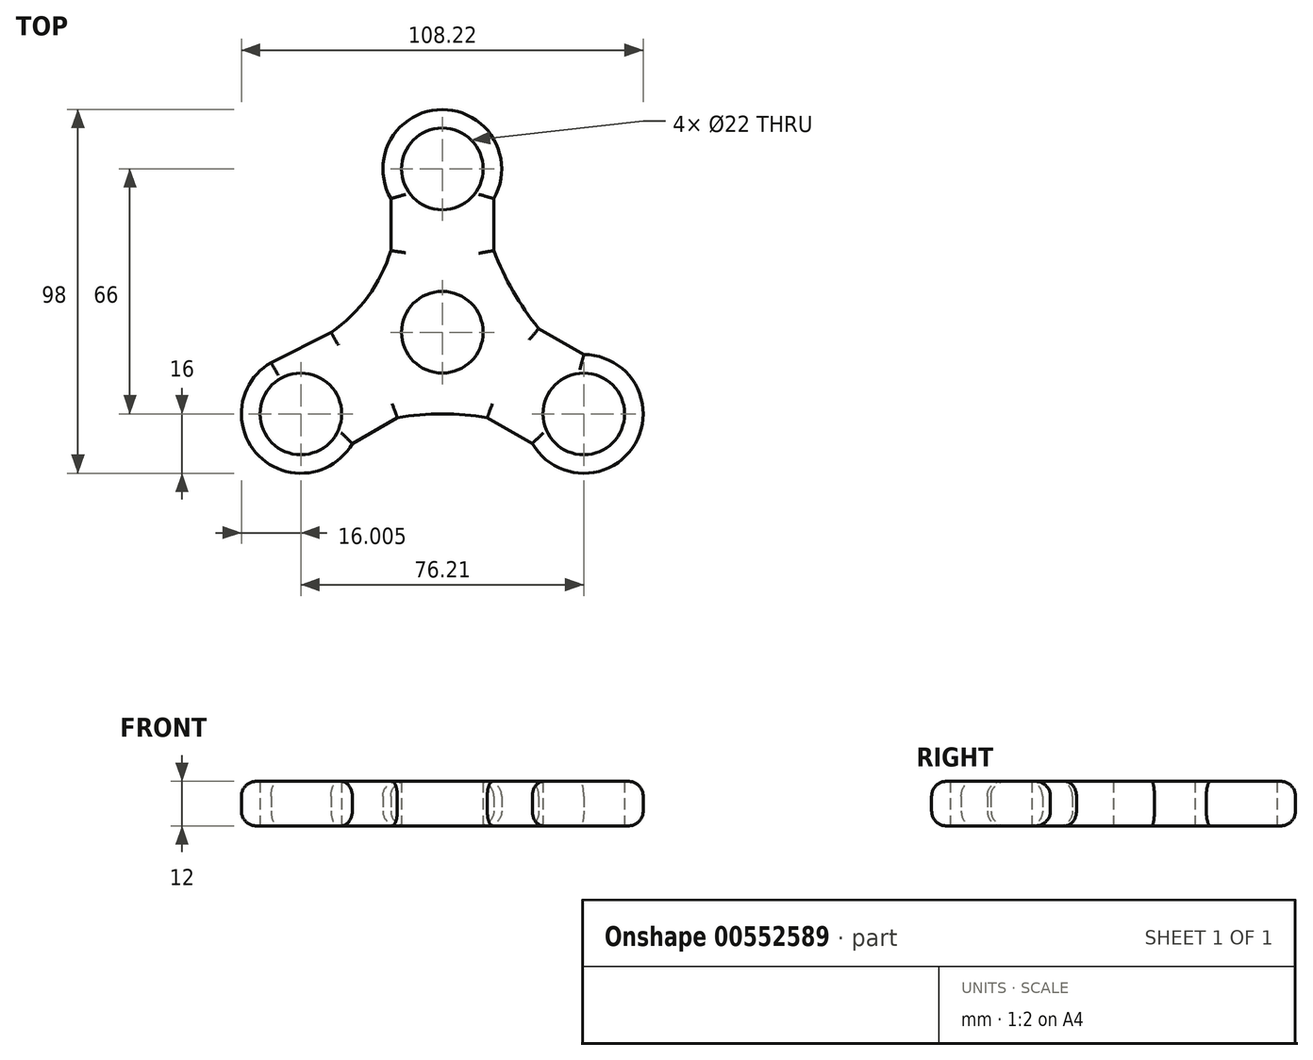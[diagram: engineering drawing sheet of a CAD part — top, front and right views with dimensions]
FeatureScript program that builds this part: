
annotation { "Feature Type Name" : "Feature", "Feature Type Description" : "" }
export const myFeature = defineFeature(function(context is Context, id is Id, definition is map)
    precondition{}
    {
        {
            var Q0;
            Q0=qCreatedBy(makeId("Top.planeOp"),FACE);
            var sketch = newSketch(context, id + "F0", { "sketchPlane" : qUnion([Q0])});
            skCircle(sketch, "E0", {"center": v(0, 0) * mm, "radius": 11 * mm});
            skLineSegment(sketch, "E1", {"start": v(0, 0) * mm, "end": v(0, 44) * mm, "construction": true});
            skCircle(sketch, "E2", {"center": v(0, 44) * mm, "radius": 11 * mm});
            skLineSegment(sketch, "E3", {"start": v(-38.1, -22) * mm, "end": v(0, 0) * mm, "construction": true});
            skLineSegment(sketch, "E4", {"start": v(38.1, -22) * mm, "end": v(0, 0) * mm, "construction": true});
            skLineSegment(sketch, "E5", {"start": v(38.1, -22) * mm, "end": v(-38.1, -22) * mm, "construction": true});
            skCircle(sketch, "E6", {"center": v(-38.1, -22) * mm, "radius": 11 * mm});
            skCircle(sketch, "E7", {"center": v(38.1, -22) * mm, "radius": 11 * mm});
            skLineSegment(sketch, "E8", {"start": v(0, 44) * mm, "end": v(-38.1, -22) * mm, "construction": true});
            skLineSegment(sketch, "E9", {"start": v(38.1, -22) * mm, "end": v(0, 44) * mm, "construction": true});
            skCircle(sketch, "E10", {"center": v(-38.1, -22) * mm, "radius": 16 * mm, "construction": true});
            skCircle(sketch, "E11", {"center": v(0, 44) * mm, "radius": 16 * mm, "construction": true});
            skCircle(sketch, "E12", {"center": v(38.1, -22) * mm, "radius": 16 * mm, "construction": true});
            skLineSegment(sketch, "E13", {"start": v(-38.1, -22) * mm, "end": v(-38.1, -6) * mm, "construction": true});
            skLineSegment(sketch, "E14", {"start": v(-38.1, -22) * mm, "end": v(-46.1, -8.14) * mm, "construction": true});
            skLineSegment(sketch, "E15", {"start": v(-38.1, -22) * mm, "end": v(-24.25, -30) * mm, "construction": true});
            skArc(sketch, "E16", {"start": v(-46.1, -8.14) * mm, "mid": v(-49.42, -33.31) * mm, "end": v(-24.25, -30) * mm});
            skLineSegment(sketch, "E17", {"start": v(0, 44) * mm, "end": v(-16, 44) * mm, "construction": true});
            skLineSegment(sketch, "E18", {"start": v(0, 44) * mm, "end": v(16, 44) * mm, "construction": true});
            skLineSegment(sketch, "E19", {"start": v(0, 44) * mm, "end": v(-13.86, 36) * mm, "construction": true});
            skCircle(sketch, "E20", {"center": v(0, 0) * mm, "radius": 16 * mm, "construction": true});
            skLineSegment(sketch, "E21", {"start": v(0, 44) * mm, "end": v(13.86, 36) * mm, "construction": true});
            skArc(sketch, "E22", {"start": v(13.86, 36) * mm, "mid": v(0, 60) * mm, "end": v(-13.86, 36) * mm});
            skLineSegment(sketch, "E23", {"start": v(38.1, -22) * mm, "end": v(38.1, -6) * mm, "construction": true});
            skLineSegment(sketch, "E24", {"start": v(38.1, -22) * mm, "end": v(24.25, -30) * mm, "construction": true});
            skArc(sketch, "E25", {"start": v(24.25, -30) * mm, "mid": v(51.96, -30) * mm, "end": v(38.1, -6) * mm});
            skLineSegment(sketch, "E26", {"start": v(-19.05, 11) * mm, "end": v(-13.86, 8) * mm, "construction": true});
            skLineSegment(sketch, "E27", {"start": v(19.05, 11) * mm, "end": v(13.86, 8) * mm, "construction": true});
            skLineSegment(sketch, "E28", {"start": v(0, -22) * mm, "end": v(0, -16) * mm, "construction": true});
            skLineSegment(sketch, "E29", {"start": v(-46.1, -8.14) * mm, "end": v(-13.86, 8) * mm});
            skLineSegment(sketch, "E30", {"start": v(-13.86, 8) * mm, "end": v(-13.86, 36) * mm});
            skLineSegment(sketch, "E31", {"start": v(13.86, 36) * mm, "end": v(13.86, 8) * mm});
            skLineSegment(sketch, "E32", {"start": v(13.86, 8) * mm, "end": v(38.1, -6) * mm});
            skLineSegment(sketch, "E33", {"start": v(24.25, -30) * mm, "end": v(0, -16) * mm});
            skLineSegment(sketch, "E34", {"start": v(0, -16) * mm, "end": v(-24.25, -30) * mm});
            skArc(sketch, "E35", {"start": v(-29.98, -0.07) * mm, "mid": v(-20.04, 9.6) * mm, "end": v(-13.86, 22) * mm});
            skArc(sketch, "E36", {"start": v(13.86, 22) * mm, "mid": v(19.05, 11) * mm, "end": v(25.98, 1) * mm});
            skArc(sketch, "E37", {"start": v(12.12, -23) * mm, "mid": v(0, -22) * mm, "end": v(-12.12, -23) * mm});
            skSolve(sketch);
        }
        {
            var Q0;
            Q0=makeQuery(id+"F0.imprint","IMPRINT",FACE,{"disambiguationData":[TD([[makeQuery(id+"F0.imprint","IMPRINT",EDGE,{"derivedFrom":sQuery(id+"F0.wireOp",EDGE,"E0")}),-1.0]])]});
            var Q1;
            {var subQ3=sQuery(id+"F0.wireOp",EDGE,"E37");Q1=makeQuery(id+"F0.imprint","IMPRINT",FACE,{"disambiguationData":[TD([[makeQuery(id+"F0.imprint","IMPRINT",EDGE,{"derivedFrom":subQ3}),-1.0]])]});}
            var Q2;
            {var subQ3=sQuery(id+"F0.wireOp",EDGE,"E35");Q2=makeQuery(id+"F0.imprint","IMPRINT",FACE,{"disambiguationData":[TD([[makeQuery(id+"F0.imprint","IMPRINT",EDGE,{"derivedFrom":subQ3}),-1.0]])]});}
            var Q3;
            {var subQ3=sQuery(id+"F0.wireOp",EDGE,"E36");Q3=makeQuery(id+"F0.imprint","IMPRINT",FACE,{"disambiguationData":[TD([[makeQuery(id+"F0.imprint","IMPRINT",EDGE,{"derivedFrom":subQ3}),-1.0]])]});}
            extrude(context, id + "F1", {"entities" : qUnion([Q0, Q1, Q2, Q3]), "depth" : 12 * mm, "offsetDistance" : 25 * mm});
        }
        {
            var Q0;
            Q0=makeQuery(id+"F1.opExtrude","CAP_EDGE",EDGE,{"disambiguationData":[OSD([sQuery(id+"F0.wireOp",EDGE,"E29")])],"isStart":false});
            var Q1;
            Q1=makeQuery(id+"F1.opExtrude","CAP_EDGE",EDGE,{"disambiguationData":[OSD([sQuery(id+"F0.wireOp",EDGE,"E34")])],"isStart":false});
            var Q2;
            Q2=makeQuery(id+"F1.opExtrude","CAP_EDGE",EDGE,{"disambiguationData":[OSD([sQuery(id+"F0.wireOp",EDGE,"E16")])],"isStart":false});
            var Q3;
            Q3=makeQuery(id+"F1.opExtrude","CAP_EDGE",EDGE,{"disambiguationData":[OSD([sQuery(id+"F0.wireOp",EDGE,"E25")])],"isStart":false});
            var Q4;
            Q4=makeQuery(id+"F1.opExtrude","CAP_EDGE",EDGE,{"disambiguationData":[OSD([sQuery(id+"F0.wireOp",EDGE,"E33")])],"isStart":false});
            var Q5;
            Q5=makeQuery(id+"F1.opExtrude","CAP_EDGE",EDGE,{"disambiguationData":[OSD([sQuery(id+"F0.wireOp",EDGE,"E32")])],"isStart":false});
            var Q6;
            Q6=makeQuery(id+"F1.opExtrude","CAP_EDGE",EDGE,{"disambiguationData":[OSD([sQuery(id+"F0.wireOp",EDGE,"E31")])],"isStart":false});
            var Q7;
            Q7=makeQuery(id+"F1.opExtrude","CAP_EDGE",EDGE,{"disambiguationData":[OSD([sQuery(id+"F0.wireOp",EDGE,"E22")])],"isStart":false});
            var Q8;
            Q8=makeQuery(id+"F1.opExtrude","CAP_EDGE",EDGE,{"disambiguationData":[OSD([sQuery(id+"F0.wireOp",EDGE,"E32")])],"isStart":true});
            var Q9;
            Q9=makeQuery(id+"F1.opExtrude","CAP_EDGE",EDGE,{"disambiguationData":[OSD([sQuery(id+"F0.wireOp",EDGE,"E29")])],"isStart":true});
            var Q10;
            Q10=makeQuery(id+"F1.opExtrude","CAP_EDGE",EDGE,{"disambiguationData":[OSD([sQuery(id+"F0.wireOp",EDGE,"E16")])],"isStart":true});
            var Q11;
            Q11=makeQuery(id+"F1.opExtrude","CAP_EDGE",EDGE,{"disambiguationData":[OSD([sQuery(id+"F0.wireOp",EDGE,"E34")])],"isStart":true});
            var Q12;
            Q12=makeQuery(id+"F1.opExtrude","CAP_EDGE",EDGE,{"disambiguationData":[OSD([sQuery(id+"F0.wireOp",EDGE,"E33")])],"isStart":true});
            var Q13;
            Q13=makeQuery(id+"F1.opExtrude","CAP_EDGE",EDGE,{"disambiguationData":[OSD([sQuery(id+"F0.wireOp",EDGE,"E25")])],"isStart":true});
            var Q14;
            Q14=makeQuery(id+"F1.opExtrude","CAP_EDGE",EDGE,{"disambiguationData":[OSD([sQuery(id+"F0.wireOp",EDGE,"E22")])],"isStart":true});
            var Q15;
            Q15=makeQuery(id+"F1.opExtrude","CAP_EDGE",EDGE,{"disambiguationData":[OSD([sQuery(id+"F0.wireOp",EDGE,"E31")])],"isStart":true});
            var Q16;
            Q16=makeQuery(id+"F1.opExtrude","CAP_EDGE",EDGE,{"disambiguationData":[OSD([sQuery(id+"F0.wireOp",EDGE,"E37")])],"isStart":false});
            var Q17;
            Q17=makeQuery(id+"F1.opExtrude","CAP_EDGE",EDGE,{"disambiguationData":[OSD([sQuery(id+"F0.wireOp",EDGE,"E35")])],"isStart":false});
            var Q18;
            Q18=makeQuery(id+"F1.opExtrude","CAP_EDGE",EDGE,{"disambiguationData":[OSD([sQuery(id+"F0.wireOp",EDGE,"E36")])],"isStart":false});
            var Q19;
            Q19=makeQuery(id+"F1.opExtrude","CAP_EDGE",EDGE,{"disambiguationData":[OSD([sQuery(id+"F0.wireOp",EDGE,"E30")])],"isStart":false});
            var Q20;
            Q20=makeQuery(id+"F1.opExtrude","CAP_EDGE",EDGE,{"disambiguationData":[OSD([sQuery(id+"F0.wireOp",EDGE,"E37")])],"isStart":true});
            var Q21;
            Q21=makeQuery(id+"F1.opExtrude","CAP_EDGE",EDGE,{"disambiguationData":[OSD([sQuery(id+"F0.wireOp",EDGE,"E36")])],"isStart":true});
            var Q22;
            Q22=makeQuery(id+"F1.opExtrude","CAP_EDGE",EDGE,{"disambiguationData":[OSD([sQuery(id+"F0.wireOp",EDGE,"E30")])],"isStart":true});
            var Q23;
            Q23=makeQuery(id+"F1.opExtrude","CAP_EDGE",EDGE,{"disambiguationData":[OSD([sQuery(id+"F0.wireOp",EDGE,"E35")])],"isStart":true});
            fillet(context, id + "F2", {"entities" : qUnion([Q0, Q1, Q2, Q3, Q4, Q5, Q6, Q7, Q8, Q9, Q10, Q11, Q12, Q13, Q14, Q15, Q16, Q17, Q18, Q19, Q20, Q21, Q22, Q23]), "radius" : 4 * mm, "tangentPropagation" : true, "allowEdgeOverflow" : false});
        }
    });
